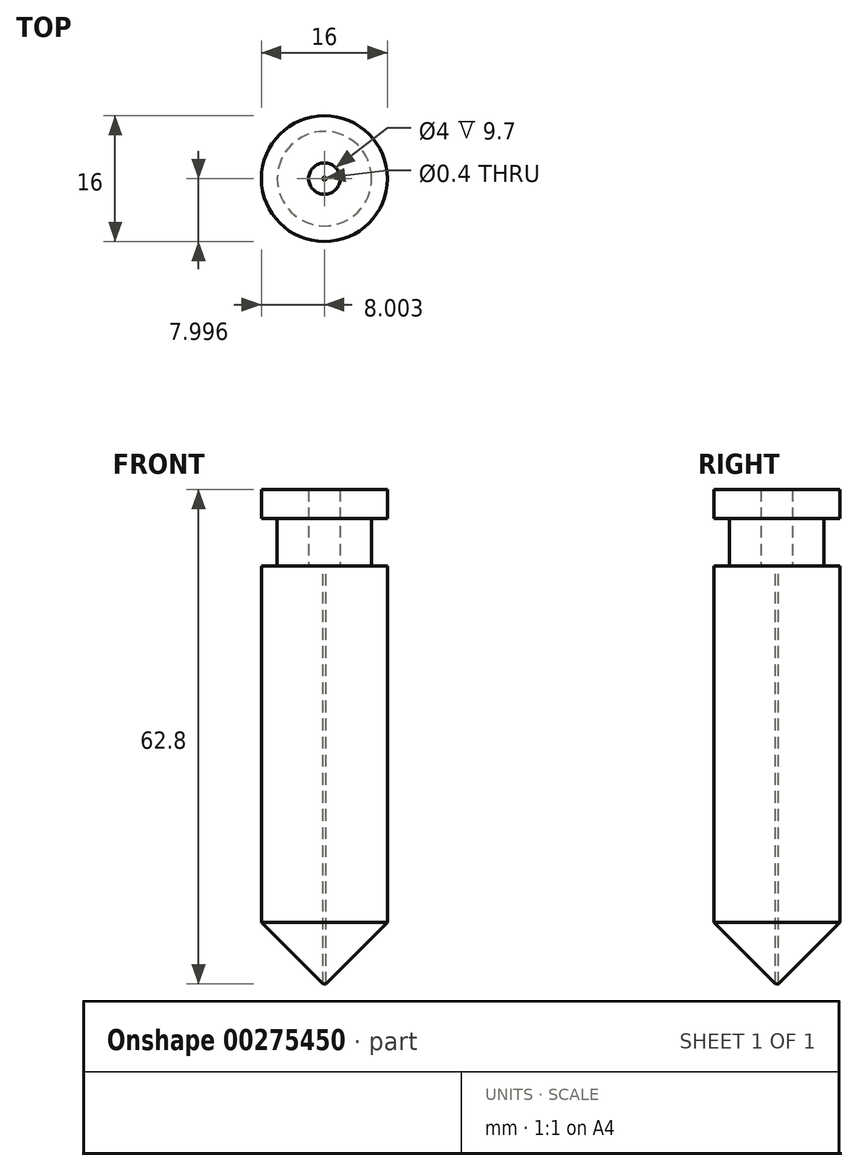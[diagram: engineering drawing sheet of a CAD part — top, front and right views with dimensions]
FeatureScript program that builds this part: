
annotation { "Feature Type Name" : "Feature", "Feature Type Description" : "" }
export const myFeature = defineFeature(function(context is Context, id is Id, definition is map)
    precondition{}
    {
        {
            var Q0;
            Q0=qCreatedBy(makeId("Top.planeOp"),FACE);
            var sketch = newSketch(context, id + "F0", { "sketchPlane" : qUnion([Q0])});
            skCircle(sketch, "E0", {"center": v(-42.4, 33.1) * mm, "radius": 8 * mm});
            skCircle(sketch, "E1", {"center": v(-42.4, 33.1) * mm, "radius": 6 * mm});
            skSolve(sketch);
        }
        {
            var Q0;
            Q0=qSketchRegion(id+"F0",true);
            var Q1;
            Q1=makeQuery(id+"F0.imprint","IMPRINT",FACE,{"disambiguationData":[TD([[makeQuery(id+"F0.imprint","IMPRINT",EDGE,{"derivedFrom":sQuery(id+"F0.wireOp",EDGE,"E1")}),1.0]])]});
            extrude(context, id + "F1", {"entities" : qUnion([Q0, Q1]), "oppositeDirection" : true, "depth" : 53.3 * mm});
        }
        {
            var Q0;
            Q0=makeQuery(id+"F0.imprint","IMPRINT",FACE,{"disambiguationData":[TD([[makeQuery(id+"F0.imprint","IMPRINT",EDGE,{"derivedFrom":sQuery(id+"F0.wireOp",EDGE,"E1")}),1.0]])]});
            extrude(context, id + "F2", {"entities" : qUnion([Q0]), "operationType" : NewBodyOperationType.ADD, "depth" : 6 * mm});
        }
        {
            var Q0;
            Q0=makeQuery(id+"F0.imprint","IMPRINT",FACE,{"disambiguationData":[TD([[makeQuery(id+"F0.imprint","IMPRINT",EDGE,{"derivedFrom":sQuery(id+"F0.wireOp",EDGE,"E0")}),1.0]])]});
            var Q1;
            Q1=makeQuery(id+"F0.imprint","IMPRINT",FACE,{"disambiguationData":[TD([[makeQuery(id+"F0.imprint","IMPRINT",EDGE,{"derivedFrom":sQuery(id+"F0.wireOp",EDGE,"E1")}),1.0]])]});
            var Q2;
            Q2=sQuery(id+"F0.wireOp",EDGE,"E0");
            var Q3;
            Q3=sQuery(id+"F0.wireOp",EDGE,"E1");
            extrude(context, id + "F3", {"entities" : qUnion([Q0, Q1]), "operationType" : NewBodyOperationType.ADD, "surfaceEntities" : qUnion([Q2, Q3]), "depth" : 9.7 * mm, "hasSecondDirection" : true, "secondDirectionOppositeDirection" : false, "secondDirectionDepth" : 6 * mm});
        }
        {
            var Q0;
            Q0=makeQuery(id+"F1.opExtrude","CAP_EDGE",EDGE,{"disambiguationData":[OSD([sQuery(id+"F0.wireOp",EDGE,"E0")])],"isStart":false});
            chamfer(context, id + "F4", {"entities" : qUnion([Q0]), "width" : 8 * mm, "tangentPropagation" : true});
        }
        {
            var Q0;
            Q0=sQuery(id+"F0.wireOp",VERTEX,"E0.center");
            var Q1;
            Q1=makeQuery(id+"F1.opExtrude","SWEPT_BODY",BODY,{"disambiguationData":[OSD([sQuery(id+"F0.wireOp",EDGE,"E0")])]});
            hole(context, id + "F5", {"style" : HoleStyle.SIMPLE, "endStyle" : HoleEndStyle.BLIND, "oppositeDirection" : true, "holeDiameter" : 4 * mm, "holeDepth" : 20 * mm, "tappedDepth" : 12 * mm, "tapClearance" : 3, "locations" : qUnion([Q0]), "scope" : qUnion([Q1])});
        }
        {
            var Q0;
            Q0=sQuery(id+"F0.wireOp",VERTEX,"E0.center");
            var Q1;
            Q1=makeQuery(id+"F1.opExtrude","SWEPT_BODY",BODY,{"disambiguationData":[OSD([sQuery(id+"F0.wireOp",EDGE,"E0")])]});
            hole(context, id + "F6", {"style" : HoleStyle.SIMPLE, "endStyle" : HoleEndStyle.BLIND, "holeDiameter" : 0.4 * mm, "holeDepth" : 70 * mm, "tappedDepth" : 12 * mm, "tapClearance" : 3, "locations" : qUnion([Q0]), "scope" : qUnion([Q1])});
        }
    });
